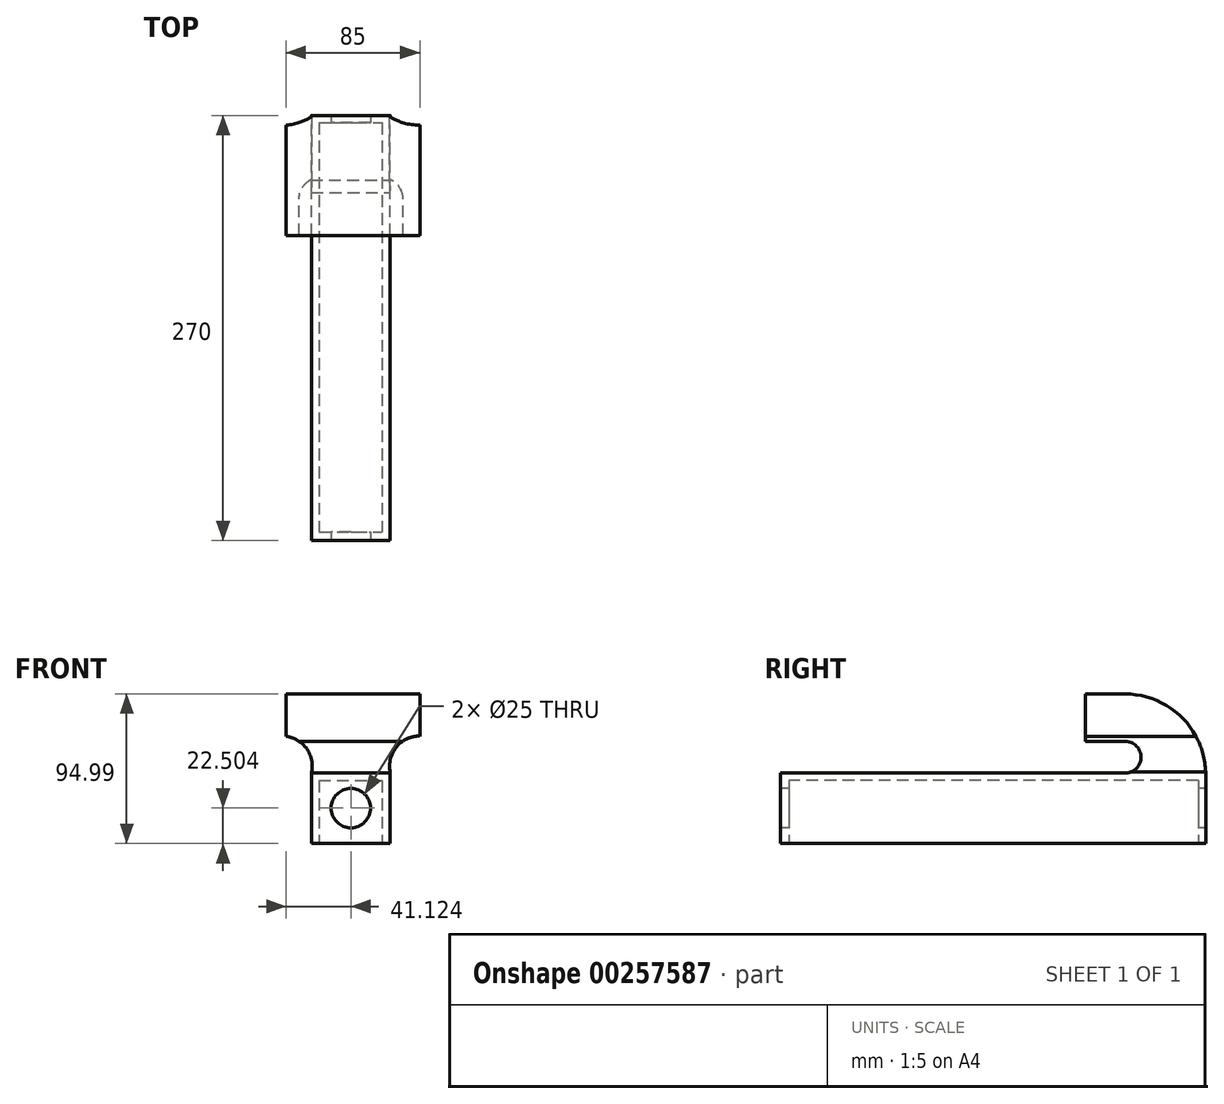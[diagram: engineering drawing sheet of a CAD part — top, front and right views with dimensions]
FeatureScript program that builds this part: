
annotation { "Feature Type Name" : "Feature", "Feature Type Description" : "" }
export const myFeature = defineFeature(function(context is Context, id is Id, definition is map)
    precondition{}
    {
        {
            var Q0;
            Q0=qCreatedBy(makeId("Right.planeOp"),FACE);
            var sketch = newSketch(context, id + "F0", { "sketchPlane" : qUnion([Q0])});
            skLineSegment(sketch, "E0", {"start": v(64.2, 19.56) * mm, "end": v(-156.83, 19.56) * mm});
            skLineSegment(sketch, "E1", {"start": v(-156.83, 19.56) * mm, "end": v(-156.83, -25.44) * mm});
            skLineSegment(sketch, "E2", {"start": v(-156.83, -25.44) * mm, "end": v(113.17, -25.44) * mm});
            skLineSegment(sketch, "E3", {"start": v(113.17, -25.44) * mm, "end": v(113.17, 19.56) * mm});
            skLineSegment(sketch, "E4", {"start": v(64.2, 19.56) * mm, "end": v(52.25, 19.56) * mm});
            skPoint(sketch, "E5.orphan", {"position": v(76.14, 19.56) * mm});
            skLineSegment(sketch, "E6", {"start": v(61.93, 39.55) * mm, "end": v(36.93, 39.55) * mm});
            skLineSegment(sketch, "E7", {"start": v(36.93, 39.55) * mm, "end": v(36.93, 69.55) * mm});
            skLineSegment(sketch, "E8", {"start": v(36.93, 69.55) * mm, "end": v(61.93, 69.55) * mm});
            skArc(sketch, "E9", {"start": v(61.93, 39.55) * mm, "mid": v(72, 30.56) * mm, "end": v(64.2, 19.56) * mm});
            skArc(sketch, "E10", {"start": v(61.93, 69.55) * mm, "mid": v(97.72, 54.98) * mm, "end": v(113.17, 19.56) * mm});
            skSolve(sketch);
        }
        {
            var Q0;
            Q0 = qSketchRegion(id + "F0", true);
            extrude(context, id + "F1", {"entities" : qUnion([Q0]), "endBound" : BoundingType.SYMMETRIC, "oppositeDirection" : true, "depth" : 85 * mm});
        }
        {
            var Q0;
            Q0=qCreatedBy(makeId("Front.planeOp"),FACE);
            var sketch = newSketch(context, id + "F2", { "sketchPlane" : qUnion([Q0])});
            skLineSegment(sketch, "E11.top", {"start": v(23.62, -36.9) * mm, "end": v(-26.38, -36.9) * mm});
            skLineSegment(sketch, "E11.left", {"start": v(23.62, 19.92) * mm, "end": v(23.62, -36.9) * mm});
            skLineSegment(sketch, "E11.right", {"start": v(-26.38, 19.92) * mm, "end": v(-26.38, -36.9) * mm});
            skArc(sketch, "E12", {"start": v(42.22, 42.8) * mm, "mid": v(27.48, 35.78) * mm, "end": v(23.62, 19.92) * mm});
            skArc(sketch, "E13", {"start": v(-26.38, 19.92) * mm, "mid": v(-30.23, 35.78) * mm, "end": v(-44.98, 42.8) * mm});
            skLineSegment(sketch, "E14", {"start": v(42.22, 42.8) * mm, "end": v(64.15, 37.74) * mm});
            skLineSegment(sketch, "E15", {"start": v(64.15, 37.74) * mm, "end": v(44.57, -67.33) * mm});
            skLineSegment(sketch, "E16", {"start": v(44.57, -67.33) * mm, "end": v(-64.05, -61.1) * mm});
            skLineSegment(sketch, "E17", {"start": v(-64.05, -61.1) * mm, "end": v(-44.98, 42.8) * mm});
            skSolve(sketch);
        }
        {
            var Q0;
            Q0 = qSketchRegion(id + "F2", true);
            extrude(context, id + "F3", {"entities" : qUnion([Q0]), "operationType" : NewBodyOperationType.REMOVE, "endBound" : BoundingType.SYMMETRIC, "depth" : 348 * mm});
        }
        {
            var Q0;
            Q0=qCreatedBy(makeId("Front.planeOp"),FACE);
            var sketch = newSketch(context, id + "F4", { "sketchPlane" : qUnion([Q0])});
            skCircle(sketch, "E18", {"center": v(-1.38, -2.94) * mm, "radius": 12.5 * mm});
            skSolve(sketch);
        }
        {
            var Q0;
            Q0 = qSketchRegion(id + "F4", true);
            extrude(context, id + "F5", {"entities" : qUnion([Q0]), "operationType" : NewBodyOperationType.REMOVE, "endBound" : BoundingType.SYMMETRIC, "oppositeDirection" : true, "depth" : 532 * mm});
        }
        {
            var Q0;
            Q0=makeQuery(id+"F1.opExtrude","SWEPT_FACE",FACE,{"disambiguationData":[OSD([sQuery(id+"F0.wireOp",EDGE,"E2")])]});
            var sketch = newSketch(context, id + "F6", { "sketchPlane" : qUnion([Q0])});
            skLineSegment(sketch, "E19.bottom", {"start": v(-21.72, -108.55) * mm, "end": v(18.28, -108.55) * mm});
            skLineSegment(sketch, "E19.top", {"start": v(-21.72, 151.45) * mm, "end": v(18.28, 151.45) * mm});
            skLineSegment(sketch, "E19.left", {"start": v(-21.72, -108.55) * mm, "end": v(-21.72, 151.45) * mm});
            skLineSegment(sketch, "E19.right", {"start": v(18.28, -108.55) * mm, "end": v(18.28, 151.45) * mm});
            skSolve(sketch);
        }
        {
            var Q0;
            Q0 = qSketchRegion(id + "F6", true);
            extrude(context, id + "F7", {"entities" : qUnion([Q0]), "operationType" : NewBodyOperationType.REMOVE, "oppositeDirection" : true, "depth" : 40 * mm});
        }
    });
